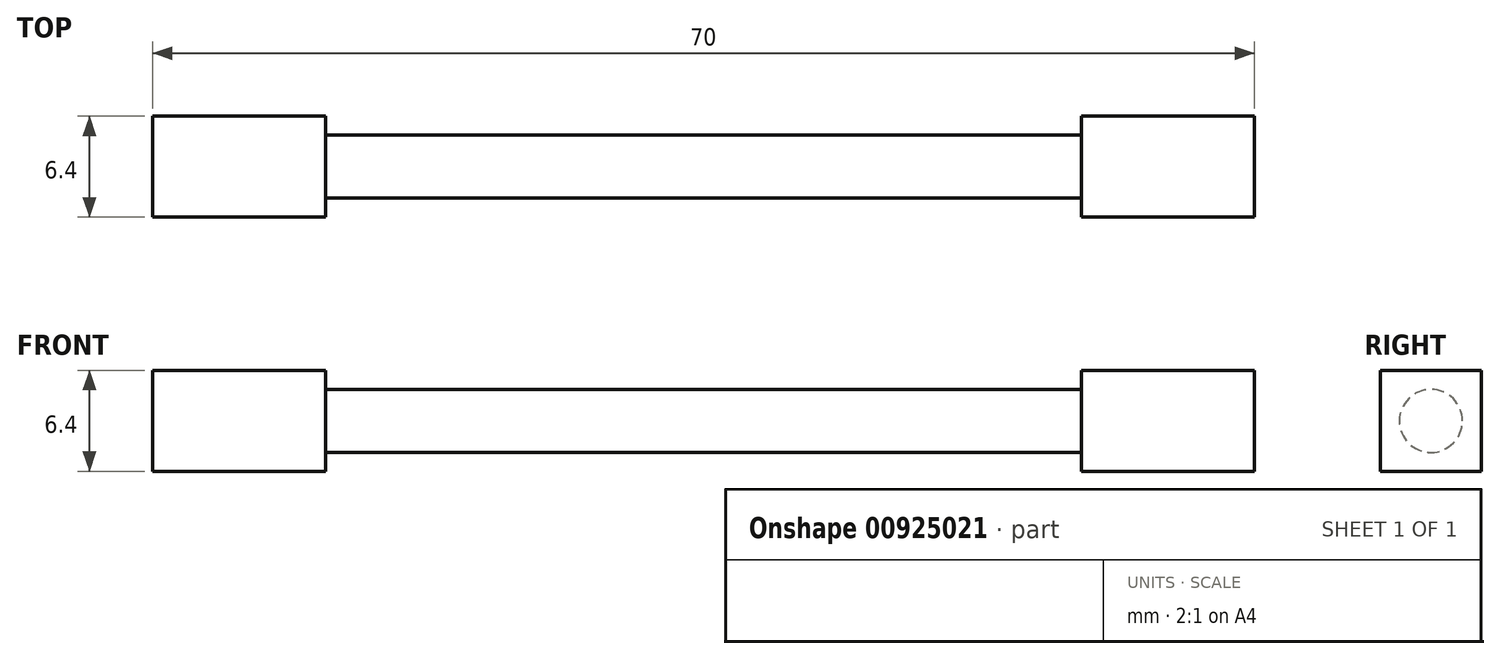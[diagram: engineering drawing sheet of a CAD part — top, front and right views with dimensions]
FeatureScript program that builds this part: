
annotation { "Feature Type Name" : "Feature", "Feature Type Description" : "" }
export const myFeature = defineFeature(function(context is Context, id is Id, definition is map)
    precondition{}
    {
        {
            var Q0;
            Q0=qCreatedBy(makeId("Front.planeOp"),FACE);
            var sketch = newSketch(context, id + "F0", { "sketchPlane" : qUnion([Q0])});
            skLineSegment(sketch, "E0.bottom", {"start": v(-35, 3.2) * mm, "end": v(35, 3.2) * mm});
            skLineSegment(sketch, "E0.top", {"start": v(-35, -3.2) * mm, "end": v(35, -3.2) * mm});
            skLineSegment(sketch, "E0.left", {"start": v(-35, 3.2) * mm, "end": v(-35, -3.2) * mm});
            skLineSegment(sketch, "E0.right", {"start": v(35, 3.2) * mm, "end": v(35, -3.2) * mm});
            skPoint(sketch, "E0.middle", {"position": v(0, 0) * mm});
            skLineSegment(sketch, "E1", {"start": v(0, 0) * mm, "end": v(24, 0) * mm});
            skLineSegment(sketch, "E2", {"start": v(24, 0) * mm, "end": v(24, 2) * mm});
            skLineSegment(sketch, "E3", {"start": v(24, 2) * mm, "end": v(-24, 2) * mm});
            skLineSegment(sketch, "E4", {"start": v(-24, 2) * mm, "end": v(-24, 0) * mm});
            skLineSegment(sketch, "E5", {"start": v(-24, 0) * mm, "end": v(0, 0) * mm});
            skLineSegment(sketch, "E6", {"start": v(-24, 3.2) * mm, "end": v(-24, -3.2) * mm});
            skLineSegment(sketch, "E7", {"start": v(24, 3.2) * mm, "end": v(24, -3.2) * mm});
            skSolve(sketch);
        }
        {
            var Q0;
            Q0=makeQuery(id+"F0.imprint","IMPRINT",FACE,{"disambiguationData":[TD([[makeQuery(id+"F0.imprint","IMPRINT",EDGE,{"derivedFrom":sQuery(id+"F0.wireOp",EDGE,"E1")}),1.0]])]});
            var Q1;
            Q1=sQuery(id+"F0.wireOp",EDGE,"E5");
            revolve(context, id + "F1", {"surfaceOperationType" : NewSurfaceOperationType.NEW, "entities" : qUnion([Q0]), "axis" : qUnion([Q1]), "revolveType" : RevolveType.FULL});
        }
        {
            var Q0;
            {var subQ1=sQuery(id+"F0.wireOp",EDGE,"E0.left");Q0=makeQuery(id+"F0.imprint","IMPRINT",FACE,{"disambiguationData":[TD([[makeQuery(id+"F0.imprint","IMPRINT",EDGE,{"derivedFrom":subQ1}),1.0]])]});}
            extrude(context, id + "F2", {"entities" : qUnion([Q0]), "endBound" : BoundingType.SYMMETRIC, "depth" : 6.4 * mm, "offsetDistance" : 25 * mm});
        }
        {
            var Q0;
            {var subQ0=sQuery(id+"F0.wireOp",EDGE,"E0.right");Q0=makeQuery(id+"F0.imprint","IMPRINT",FACE,{"disambiguationData":[TD([[makeQuery(id+"F0.imprint","IMPRINT",EDGE,{"derivedFrom":subQ0}),-1.0]])]});}
            extrude(context, id + "F3", {"entities" : qUnion([Q0]), "endBound" : BoundingType.SYMMETRIC, "depth" : 6.4 * mm, "offsetDistance" : 25 * mm});
        }
        {
            var Q0;
            Q0=makeQuery(id+"F2.opExtrude","CAP_VERTEX",VERTEX,{"disambiguationData":[OSD([sQuery(id+"F0.wireOp",EDGE,"E0.bottom"),sQuery(id+"F0.wireOp",EDGE,"E6")])],"isStart":false});
            var Q1;
            Q1=makeQuery(id+"F2.opExtrude","CAP_VERTEX",VERTEX,{"disambiguationData":[OSD([sQuery(id+"F0.wireOp",EDGE,"E0.bottom"),sQuery(id+"F0.wireOp",EDGE,"E0.left")])],"isStart":false});
            var Q2;
            Q2=makeQuery(id+"F2.opExtrude","CAP_VERTEX",VERTEX,{"disambiguationData":[OSD([sQuery(id+"F0.wireOp",EDGE,"E0.top"),sQuery(id+"F0.wireOp",EDGE,"E6")])],"isStart":true});
            cPlane(context, id + "F4", {"entities" : qUnion([Q0, Q1, Q2]), "cplaneType" : CPlaneType.THREE_POINT, "offset" : 25 * mm, "width" : 150 * mm, "height" : 150 * mm});
        }
    });
